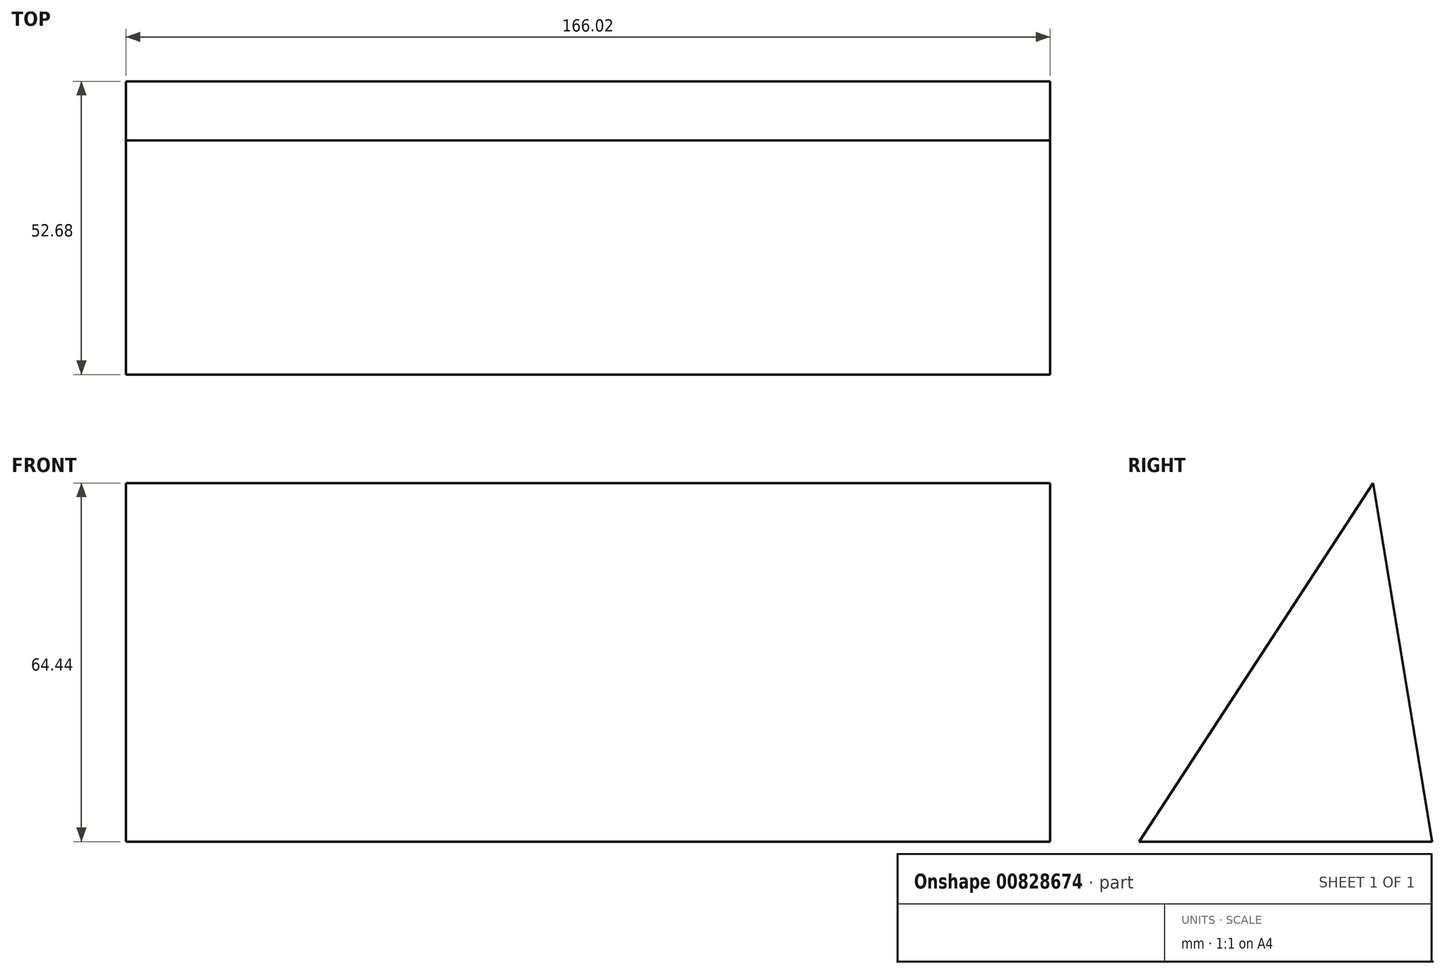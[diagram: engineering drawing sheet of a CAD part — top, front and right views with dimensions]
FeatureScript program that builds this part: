
annotation { "Feature Type Name" : "Feature", "Feature Type Description" : "" }
export const myFeature = defineFeature(function(context is Context, id is Id, definition is map)
    precondition{}
    {
        {
            var Q0;
            Q0=qCreatedBy(makeId("Right.planeOp"),FACE);
            var sketch = newSketch(context, id + "F0", { "sketchPlane" : qUnion([Q0])});
            skLineSegment(sketch, "E0", {"start": v(10.62, -11.2) * mm, "end": v(-42.06, -11.2) * mm});
            skLineSegment(sketch, "E1", {"start": v(-42.06, -11.2) * mm, "end": v(0, 53.24) * mm});
            skLineSegment(sketch, "E2", {"start": v(0, 53.24) * mm, "end": v(10.62, -11.2) * mm});
            skSolve(sketch);
        }
        {
            var Q0;
            Q0=makeQuery(id+"F0.imprint","IMPRINT",FACE,{"disambiguationData":[TD([[makeQuery(id+"F0.imprint","IMPRINT",EDGE,{"derivedFrom":sQuery(id+"F0.wireOp",EDGE,"E0")}),-1.0]])]});
            var sketch = newSketch(context, id + "F1", { "sketchPlane" : qUnion([Q0])});
            skSolve(sketch);
        }
        {
            var Q0;
            Q0=makeQuery(id+"F1.imprint","IMPRINT",FACE,{"disambiguationData":[TD([[makeQuery(id+"F1.imprint","IMPRINT",EDGE,{"derivedFrom":makeQuery(id+"F0.imprint","IMPRINT",EDGE,{"derivedFrom":sQuery(id+"F0.wireOp",EDGE,"E0")})}),-1.0]])]});
            extrude(context, id + "F2", {"entities" : qUnion([Q0]), "depth" : 166.02 * mm, "offsetDistance" : 25 * mm});
        }
    });
